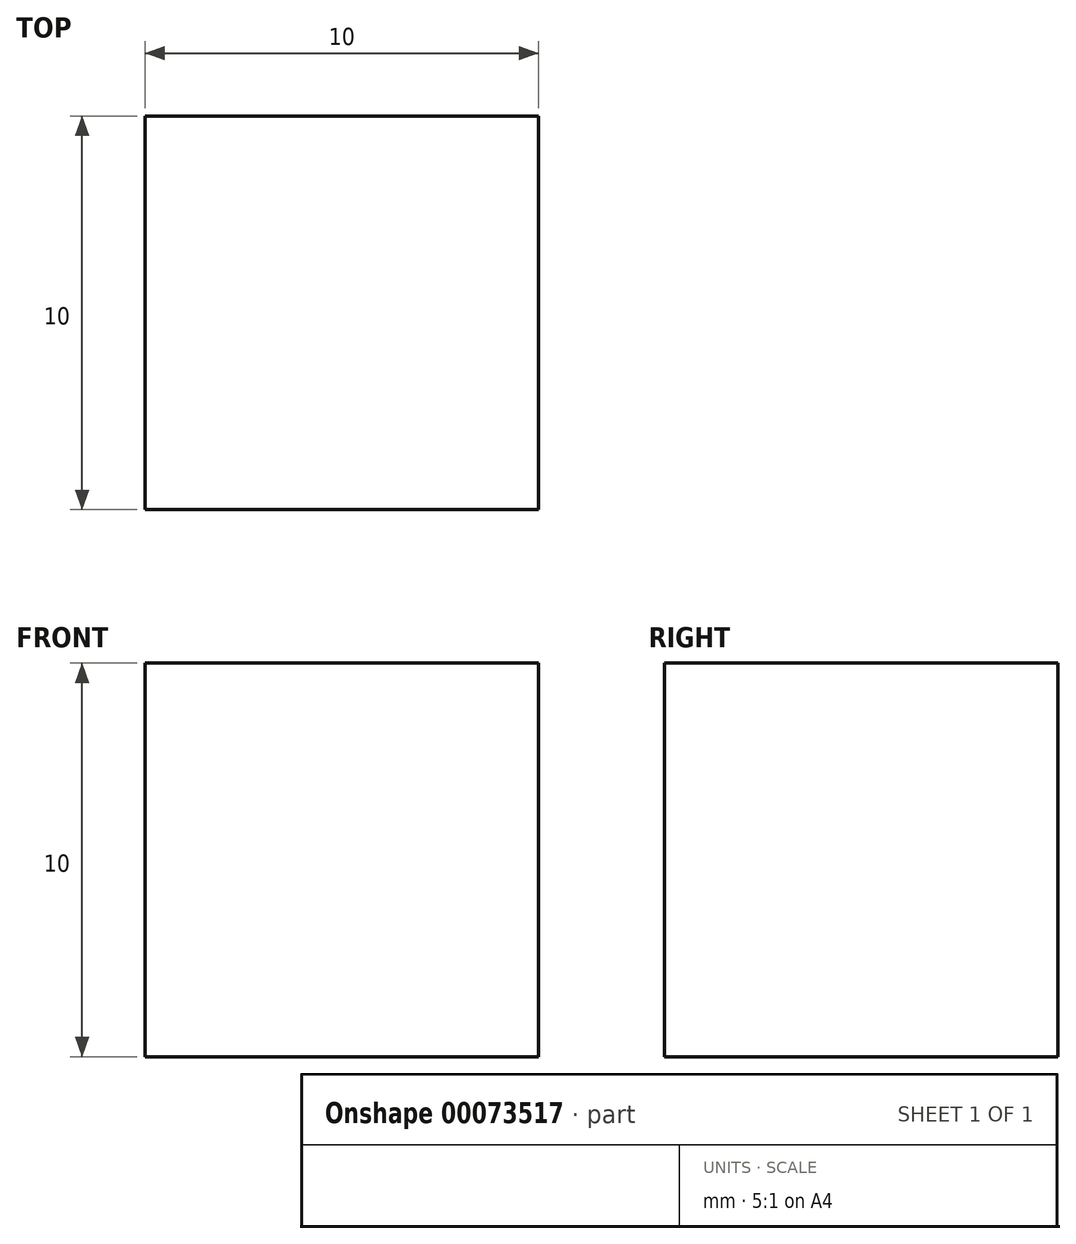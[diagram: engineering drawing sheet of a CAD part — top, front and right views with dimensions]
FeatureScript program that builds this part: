
annotation { "Feature Type Name" : "Feature", "Feature Type Description" : "" }
export const myFeature = defineFeature(function(context is Context, id is Id, definition is map)
    precondition{}
    {
        {
            var Q0;
            Q0=qCreatedBy(makeId("Top.planeOp"),FACE);
            var sketch = newSketch(context, id + "F0", { "sketchPlane" : qUnion([Q0])});
            skLineSegment(sketch, "E0.rect.bottom", {"start": v(-49.06, 4.45) * mm, "end": v(-59.06, 4.45) * mm});
            skLineSegment(sketch, "E0.rect.top", {"start": v(-49.06, 14.45) * mm, "end": v(-59.06, 14.45) * mm});
            skLineSegment(sketch, "E0.rect.left", {"start": v(-49.06, 4.45) * mm, "end": v(-49.06, 14.45) * mm});
            skLineSegment(sketch, "E0.rect.right", {"start": v(-59.06, 4.45) * mm, "end": v(-59.06, 14.45) * mm});
            skPoint(sketch, "E0.rect.middle", {"position": v(-54.06, 9.45) * mm});
            skSolve(sketch);
        }
        {
            var Q0;
            Q0 = qSketchRegion(id + "F0", true);
            extrude(context, id + "F1", {"entities" : qUnion([Q0]), "depth" : 10 * mm});
        }
    });
